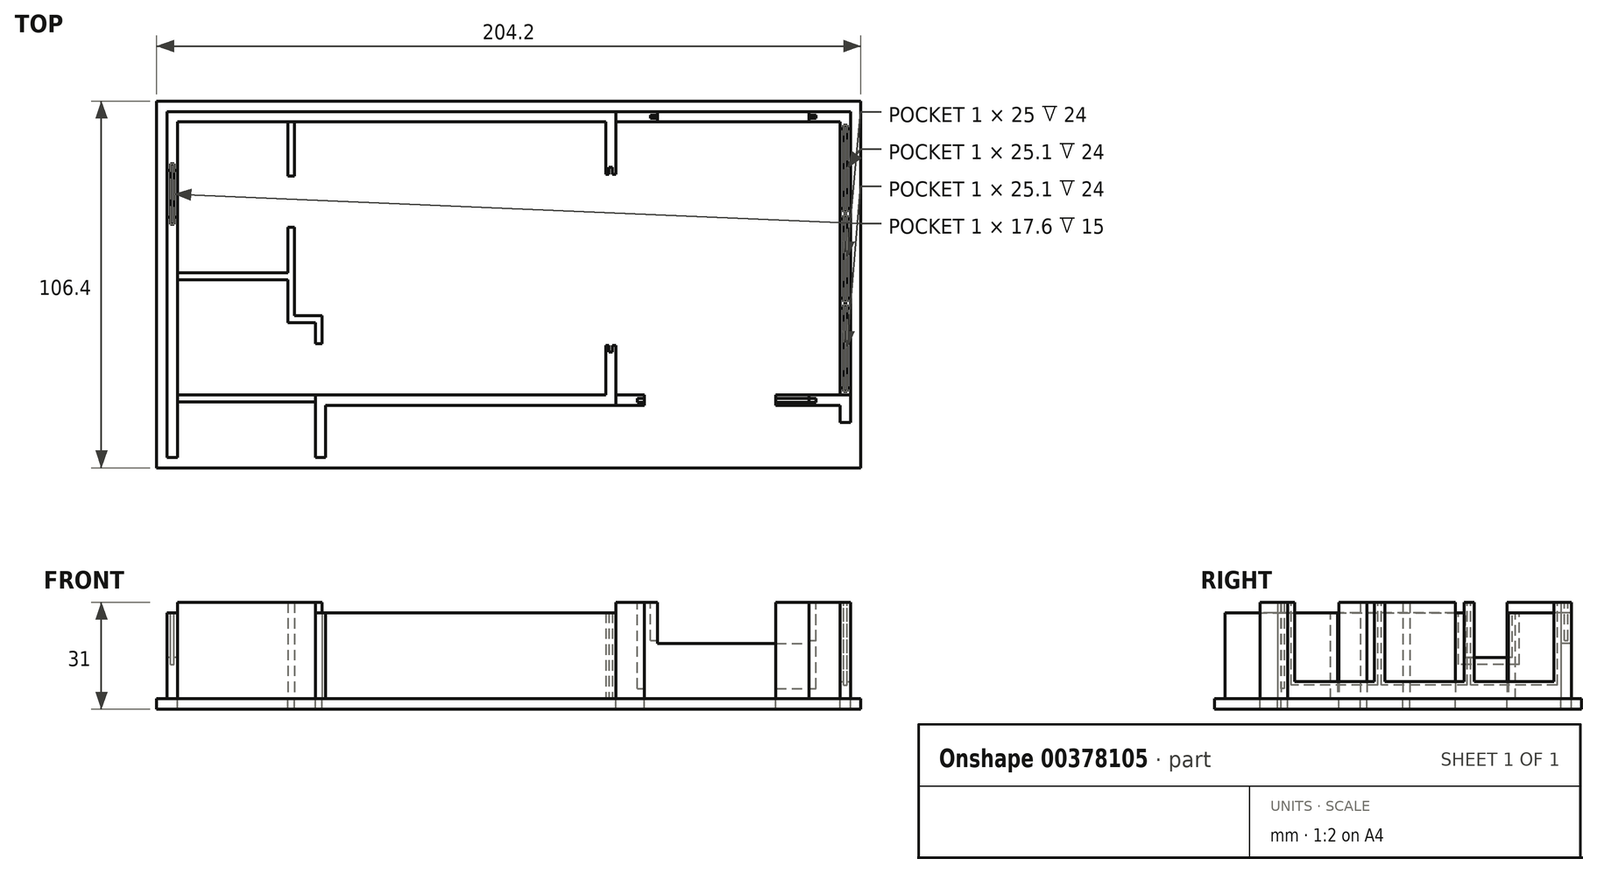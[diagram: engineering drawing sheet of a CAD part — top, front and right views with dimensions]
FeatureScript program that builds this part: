
annotation { "Feature Type Name" : "Feature", "Feature Type Description" : "" }
export const myFeature = defineFeature(function(context is Context, id is Id, definition is map)
    precondition{}
    {
        {
            var Q0;
            Q0=qCreatedBy(makeId("Top.planeOp"),FACE);
            var sketch = newSketch(context, id + "F0", { "sketchPlane" : qUnion([Q0])});
            skLineSegment(sketch, "E0.bottom", {"start": v(-6, 6) * mm, "end": v(198.2, 6) * mm});
            skLineSegment(sketch, "E0.top", {"start": v(-6, -100.4) * mm, "end": v(198.2, -100.4) * mm});
            skLineSegment(sketch, "E0.left", {"start": v(-6, 6) * mm, "end": v(-6, -100.4) * mm});
            skLineSegment(sketch, "E0.right", {"start": v(198.2, 6) * mm, "end": v(198.2, -100.4) * mm});
            skSolve(sketch);
        }
        {
            var Q0;
            Q0 = qSketchRegion(id + "F0", true);
            extrude(context, id + "F1", {"entities" : qUnion([Q0]), "oppositeDirection" : true, "depth" : 3 * mm});
        }
        {
            var Q0;
            Q0=qCreatedBy(makeId("Top.planeOp"),FACE);
            var sketch = newSketch(context, id + "F2", { "sketchPlane" : qUnion([Q0])});
            skLineSegment(sketch, "E1.bottom", {"start": v(0, 0) * mm, "end": v(124.2, 0) * mm});
            skLineSegment(sketch, "E1.top", {"start": v(40, -79.2) * mm, "end": v(124.2, -79.2) * mm});
            skLineSegment(sketch, "E1.left", {"start": v(0, 0) * mm, "end": v(0, -79.2) * mm});
            skLineSegment(sketch, "E2", {"start": v(124.2, 0) * mm, "end": v(124.2, -15.2) * mm});
            skLineSegment(sketch, "E3", {"start": v(124.2, -79.2) * mm, "end": v(124.2, -64.8) * mm});
            skLineSegment(sketch, "E4", {"start": v(0, -43.8) * mm, "end": v(34, -43.8) * mm, "construction": true});
            skLineSegment(sketch, "E5", {"start": v(34, -43.8) * mm, "end": v(34, -30.6) * mm, "construction": true});
            skLineSegment(sketch, "E6", {"start": v(34, 0) * mm, "end": v(34, -15.6) * mm, "construction": true});
            skLineSegment(sketch, "E7", {"start": v(34, -43.8) * mm, "end": v(34, -56.2) * mm, "construction": true});
            skLineSegment(sketch, "E8", {"start": v(0, -56.2) * mm, "end": v(40, -56.2) * mm, "construction": true});
            skLineSegment(sketch, "E9", {"start": v(40, -56.2) * mm, "end": v(40, -64.4) * mm, "construction": true});
            skLineSegment(sketch, "E10", {"start": v(40, -79.2) * mm, "end": v(40, -97.4) * mm});
            skLineSegment(sketch, "E11", {"start": v(0, -79.2) * mm, "end": v(0, -97.4) * mm});
            skLineSegment(sketch, "E12", {"start": v(0, -97.4) * mm, "end": v(40, -97.4) * mm, "construction": true});
            skLineSegment(sketch, "E13.0", {"start": v(-3, 3) * mm, "end": v(127.2, 3) * mm});
            skLineSegment(sketch, "E14.0", {"start": v(-3, 0) * mm, "end": v(-3, -79.2) * mm});
            skLineSegment(sketch, "E15.0", {"start": v(-3, -79.2) * mm, "end": v(-3, -97.4) * mm});
            skLineSegment(sketch, "E16.0", {"start": v(43, -82.2) * mm, "end": v(43, -97.4) * mm});
            skLineSegment(sketch, "E17.0", {"start": v(43, -82.2) * mm, "end": v(127.2, -82.2) * mm});
            skLineSegment(sketch, "E18.0", {"start": v(127.2, -82.34) * mm, "end": v(127.2, -64.8) * mm});
            skLineSegment(sketch, "E19", {"start": v(-3, -97.4) * mm, "end": v(0, -97.4) * mm});
            skLineSegment(sketch, "E20", {"start": v(40, -97.4) * mm, "end": v(43, -97.4) * mm});
            skLineSegment(sketch, "E21.0", {"start": v(127.2, 3.04) * mm, "end": v(127.2, -15.2) * mm});
            skLineSegment(sketch, "E22", {"start": v(124.2, -15.2) * mm, "end": v(127.2, -15.2) * mm});
            skLineSegment(sketch, "E23", {"start": v(-3, 0) * mm, "end": v(-3, 3) * mm});
            skPoint(sketch, "E24.orphan", {"position": v(0, 3) * mm});
            skLineSegment(sketch, "E25", {"start": v(124.2, -64.8) * mm, "end": v(127.2, -64.8) * mm});
            skSolve(sketch);
        }
        {
            var Q0;
            Q0=makeQuery(id+"F2.imprint","IMPRINT",FACE,{"disambiguationData":[TD([[makeQuery(id+"F2.imprint","IMPRINT",EDGE,{"derivedFrom":sQuery(id+"F2.wireOp",EDGE,"E1.bottom")}),1.0]])]});
            var Q1;
            Q1=makeQuery(id+"F2.imprint","IMPRINT",FACE,{"disambiguationData":[TD([[makeQuery(id+"F2.imprint","IMPRINT",EDGE,{"derivedFrom":sQuery(id+"F2.wireOp",EDGE,"E1.top")}),-1.0]])]});
            extrude(context, id + "F3", {"entities" : qUnion([Q0, Q1]), "operationType" : NewBodyOperationType.ADD, "depth" : 25 * mm});
        }
        {
            var Q0;
            Q0=qCreatedBy(makeId("Top.planeOp"),FACE);
            var sketch = newSketch(context, id + "F4", { "sketchPlane" : qUnion([Q0])});
            skLineSegment(sketch, "E26", {"start": v(0, -43.8) * mm, "end": v(32, -43.8) * mm});
            skLineSegment(sketch, "E27", {"start": v(34, 0) * mm, "end": v(34, -15.65) * mm});
            skLineSegment(sketch, "E28", {"start": v(34, -30.6) * mm, "end": v(34, -56.2) * mm});
            skLineSegment(sketch, "E29", {"start": v(34, -56.2) * mm, "end": v(42, -56.2) * mm});
            skLineSegment(sketch, "E30.0", {"start": v(32, 0) * mm, "end": v(32, -15.65) * mm});
            skLineSegment(sketch, "E31", {"start": v(32, 0) * mm, "end": v(34, 0) * mm});
            skLineSegment(sketch, "E32", {"start": v(32, -15.65) * mm, "end": v(34, -15.65) * mm});
            skLineSegment(sketch, "E33.0", {"start": v(32, -30.6) * mm, "end": v(32, -43.8) * mm});
            skLineSegment(sketch, "E34.0", {"start": v(0, -45.8) * mm, "end": v(32, -45.8) * mm});
            skLineSegment(sketch, "E35.0", {"start": v(32, -58.2) * mm, "end": v(40, -58.2) * mm});
            skLineSegment(sketch, "E36", {"start": v(32, -30.6) * mm, "end": v(34, -30.6) * mm});
            skLineSegment(sketch, "E37", {"start": v(0, -43.8) * mm, "end": v(0, -45.8) * mm});
            skPoint(sketch, "E38.orphan", {"position": v(34, -43.8) * mm});
            skLineSegment(sketch, "E39.trimOffspring", {"start": v(32, -45.8) * mm, "end": v(32, -58.2) * mm});
            skPoint(sketch, "E40.orphan", {"position": v(0, -56.2) * mm});
            skLineSegment(sketch, "E41.0", {"start": v(42, -56.2) * mm, "end": v(42, -64.4) * mm});
            skLineSegment(sketch, "E42", {"start": v(40, -64.4) * mm, "end": v(40, -58.2) * mm});
            skLineSegment(sketch, "E43", {"start": v(40, -64.4) * mm, "end": v(42, -64.4) * mm});
            skSolve(sketch);
        }
        {
            var Q0;
            Q0=makeQuery(id+"F4.imprint","IMPRINT",FACE,{"disambiguationData":[TD([[makeQuery(id+"F4.imprint","IMPRINT",EDGE,{"derivedFrom":sQuery(id+"F4.wireOp",EDGE,"E26")}),-1.0]])]});
            var Q1;
            Q1=makeQuery(id+"F4.imprint","IMPRINT",FACE,{"disambiguationData":[TD([[makeQuery(id+"F4.imprint","IMPRINT",EDGE,{"derivedFrom":sQuery(id+"F4.wireOp",EDGE,"E27")}),-1.0]])]});
            extrude(context, id + "F5", {"entities" : qUnion([Q0, Q1]), "depth" : 28 * mm});
        }
        {
            var Q0;
            Q0=qCreatedBy(makeId("Top.planeOp"),FACE);
            var sketch = newSketch(context, id + "F6", { "sketchPlane" : qUnion([Q0])});
            skLineSegment(sketch, "E44", {"start": v(127.2, -82.2) * mm, "end": v(135.4, -82.2) * mm});
            skLineSegment(sketch, "E45", {"start": v(183.2, -82.2) * mm, "end": v(192.2, -82.2) * mm});
            skLineSegment(sketch, "E46", {"start": v(192.2, -82.2) * mm, "end": v(192.2, -87.2) * mm});
            skLineSegment(sketch, "E47.0", {"start": v(127.2, -79.2) * mm, "end": v(135.4, -79.2) * mm});
            skLineSegment(sketch, "E48", {"start": v(135.4, -79.2) * mm, "end": v(135.4, -82.2) * mm});
            skLineSegment(sketch, "E49.0", {"start": v(183.2, -79.2) * mm, "end": v(195.2, -79.2) * mm});
            skLineSegment(sketch, "E50.0", {"start": v(195.2, -79.2) * mm, "end": v(195.2, -87.2) * mm});
            skLineSegment(sketch, "E51", {"start": v(183.2, -79.2) * mm, "end": v(183.2, -82.2) * mm});
            skLineSegment(sketch, "E52", {"start": v(192.2, -87.2) * mm, "end": v(195.2, -87.2) * mm});
            skLineSegment(sketch, "E53", {"start": v(127.2, -79.2) * mm, "end": v(127.2, -82.2) * mm});
            skSolve(sketch);
        }
        {
            var Q0;
            Q0=makeQuery(id+"F6.imprint","IMPRINT",FACE,{"disambiguationData":[TD([[makeQuery(id+"F6.imprint","IMPRINT",EDGE,{"derivedFrom":sQuery(id+"F6.wireOp",EDGE,"E45")}),1.0]])]});
            var Q1;
            Q1=makeQuery(id+"F6.imprint","IMPRINT",FACE,{"disambiguationData":[TD([[makeQuery(id+"F6.imprint","IMPRINT",EDGE,{"derivedFrom":sQuery(id+"F6.wireOp",EDGE,"E44")}),1.0]])]});
            extrude(context, id + "F7", {"entities" : qUnion([Q0, Q1]), "depth" : 28 * mm});
        }
        {
            var Q0;
            Q0=makeQuery(id+"F3.opExtrude","SWEPT_FACE",FACE,{"disambiguationData":[OSD([sQuery(id+"F2.wireOp",EDGE,"E14.0"),sQuery(id+"F2.wireOp",EDGE,"E15.0"),sQuery(id+"F2.wireOp",EDGE,"E23")])]});
            var sketch = newSketch(context, id + "F8", { "sketchPlane" : qUnion([Q0])});
            skLineSegment(sketch, "E54.bottom", {"start": v(14.1, 25) * mm, "end": v(27.7, 25) * mm});
            skLineSegment(sketch, "E54.top", {"start": v(14.1, 12) * mm, "end": v(27.7, 12) * mm});
            skLineSegment(sketch, "E54.left", {"start": v(14.1, 25) * mm, "end": v(14.1, 12) * mm});
            skLineSegment(sketch, "E54.right", {"start": v(27.7, 25) * mm, "end": v(27.7, 12) * mm});
            skSolve(sketch);
        }
        {
            var Q0;
            Q0 = qSketchRegion(id + "F8", true);
            extrude(context, id + "F9", {"entities" : qUnion([Q0]), "operationType" : NewBodyOperationType.REMOVE, "oppositeDirection" : true, "depth" : 3 * mm});
        }
        {
            var Q0;
            Q0=qCreatedBy(makeId("Top.planeOp"),FACE);
            var sketch = newSketch(context, id + "F10", { "sketchPlane" : qUnion([Q0])});
            skLineSegment(sketch, "E55.bottom", {"start": v(40, -79.2) * mm, "end": v(0, -79.2) * mm});
            skLineSegment(sketch, "E55.top", {"start": v(40, -81.2) * mm, "end": v(0, -81.2) * mm});
            skLineSegment(sketch, "E55.left", {"start": v(40, -79.2) * mm, "end": v(40, -81.2) * mm});
            skLineSegment(sketch, "E55.right", {"start": v(0, -79.2) * mm, "end": v(0, -81.2) * mm});
            skSolve(sketch);
        }
        {
            var Q0;
            Q0=makeQuery(id+"F10.imprint","IMPRINT",FACE,{"disambiguationData":[TD([[makeQuery(id+"F10.imprint","IMPRINT",EDGE,{"derivedFrom":sQuery(id+"F10.wireOp",EDGE,"E55.bottom")}),1.0]])]});
            extrude(context, id + "F11", {"entities" : qUnion([Q0]), "depth" : 28 * mm});
        }
        {
            var Q0;
            Q0=qCreatedBy(makeId("Top.planeOp"),FACE);
            var sketch = newSketch(context, id + "F12", { "sketchPlane" : qUnion([Q0])});
            skLineSegment(sketch, "E56.bottom", {"start": v(127.2, 3) * mm, "end": v(195.2, 3) * mm});
            skLineSegment(sketch, "E56.top", {"start": v(127.2, 0) * mm, "end": v(195.2, 0) * mm});
            skLineSegment(sketch, "E56.left", {"start": v(127.2, 3) * mm, "end": v(127.2, 0) * mm});
            skPoint(sketch, "E57.orphan", {"position": v(185.9, 0) * mm});
            skLineSegment(sketch, "E58", {"start": v(195.2, 0) * mm, "end": v(195.2, 3) * mm});
            skSolve(sketch);
        }
        {
            var Q0;
            Q0=makeQuery(id+"F12.imprint","IMPRINT",FACE,{"disambiguationData":[TD([[makeQuery(id+"F12.imprint","IMPRINT",EDGE,{"derivedFrom":sQuery(id+"F12.wireOp",EDGE,"E56.bottom")}),-1.0]])]});
            extrude(context, id + "F13", {"entities" : qUnion([Q0]), "depth" : 28 * mm});
        }
        {
            var Q0;
            Q0=makeQuery(id+"F13.opExtrude","SWEPT_FACE",FACE,{"disambiguationData":[OSD([sQuery(id+"F12.wireOp",EDGE,"E56.top")])]});
            var sketch = newSketch(context, id + "F14", { "sketchPlane" : qUnion([Q0])});
            skLineSegment(sketch, "E59.bottom", {"start": v(139.2, 28) * mm, "end": v(183.2, 28) * mm});
            skLineSegment(sketch, "E59.top", {"start": v(139.2, 16) * mm, "end": v(183.2, 16) * mm});
            skLineSegment(sketch, "E59.left", {"start": v(139.2, 28) * mm, "end": v(139.2, 16) * mm});
            skLineSegment(sketch, "E59.right", {"start": v(183.2, 28) * mm, "end": v(183.2, 16) * mm});
            skSolve(sketch);
        }
        {
            var Q0;
            Q0=makeQuery(id+"F14.imprint","IMPRINT",FACE,{"disambiguationData":[TD([[makeQuery(id+"F14.imprint","IMPRINT",EDGE,{"derivedFrom":sQuery(id+"F14.wireOp",EDGE,"E59.bottom")}),-1.0]])]});
            extrude(context, id + "F15", {"entities" : qUnion([Q0]), "operationType" : NewBodyOperationType.REMOVE, "oppositeDirection" : true, "depth" : 3 * mm});
        }
        {
            var Q0;
            Q0=qCreatedBy(makeId("Top.planeOp"),FACE);
            var sketch = newSketch(context, id + "F16", { "sketchPlane" : qUnion([Q0])});
            skLineSegment(sketch, "E60.bottom", {"start": v(192.2, 0) * mm, "end": v(195.2, 0) * mm});
            skLineSegment(sketch, "E60.top", {"start": v(192.2, -79.2) * mm, "end": v(195.2, -79.2) * mm});
            skLineSegment(sketch, "E60.left", {"start": v(192.2, 0) * mm, "end": v(192.2, -79.2) * mm});
            skLineSegment(sketch, "E60.right", {"start": v(195.2, 0) * mm, "end": v(195.2, -79.2) * mm});
            skSolve(sketch);
        }
        {
            var Q0;
            Q0=makeQuery(id+"F16.imprint","IMPRINT",FACE,{"disambiguationData":[TD([[makeQuery(id+"F16.imprint","IMPRINT",EDGE,{"derivedFrom":sQuery(id+"F16.wireOp",EDGE,"E60.bottom")}),-1.0]])]});
            extrude(context, id + "F17", {"entities" : qUnion([Q0]), "depth" : 5 * mm});
        }
        {
            var Q0;
            Q0=makeQuery(id+"F17.opExtrude","CAP_FACE",FACE,{"disambiguationData":[OSD([sQuery(id+"F16.wireOp",EDGE,"E60.bottom"),sQuery(id+"F16.wireOp",EDGE,"E60.top"),sQuery(id+"F16.wireOp",EDGE,"E60.left"),sQuery(id+"F16.wireOp",EDGE,"E60.right")])],"isStart":false});
            var sketch = newSketch(context, id + "F18", { "sketchPlane" : qUnion([Q0])});
            skLineSegment(sketch, "E61.bottom", {"start": v(192.2, 0) * mm, "end": v(195.2, 0) * mm});
            skLineSegment(sketch, "E61.top", {"start": v(192.2, -2) * mm, "end": v(195.2, -2) * mm});
            skLineSegment(sketch, "E61.left", {"start": v(192.2, 0) * mm, "end": v(192.2, -2) * mm});
            skLineSegment(sketch, "E61.right", {"start": v(195.2, 0) * mm, "end": v(195.2, -2) * mm});
            skLineSegment(sketch, "E62.bottom", {"start": v(192.2, -79.2) * mm, "end": v(195.2, -79.2) * mm});
            skLineSegment(sketch, "E62.top", {"start": v(192.2, -77.2) * mm, "end": v(195.2, -77.2) * mm});
            skLineSegment(sketch, "E62.left", {"start": v(192.2, -79.2) * mm, "end": v(192.2, -77.2) * mm});
            skLineSegment(sketch, "E62.right", {"start": v(195.2, -79.2) * mm, "end": v(195.2, -77.2) * mm});
            skLineSegment(sketch, "E63.bottom", {"start": v(192.2, -54.1) * mm, "end": v(195.2, -54.1) * mm});
            skLineSegment(sketch, "E63.top", {"start": v(192.2, -51.1) * mm, "end": v(195.2, -51.1) * mm});
            skLineSegment(sketch, "E63.left", {"start": v(192.2, -54.1) * mm, "end": v(192.2, -51.1) * mm});
            skLineSegment(sketch, "E63.right", {"start": v(195.2, -54.1) * mm, "end": v(195.2, -51.1) * mm});
            skLineSegment(sketch, "E64.bottom", {"start": v(192.2, -28.1) * mm, "end": v(195.2, -28.1) * mm});
            skLineSegment(sketch, "E64.top", {"start": v(192.2, -25.1) * mm, "end": v(195.2, -25.1) * mm});
            skLineSegment(sketch, "E64.left", {"start": v(192.2, -28.1) * mm, "end": v(192.2, -25.1) * mm});
            skLineSegment(sketch, "E64.right", {"start": v(195.2, -28.1) * mm, "end": v(195.2, -25.1) * mm});
            skSolve(sketch);
        }
        {
            var Q0;
            Q0 = qSketchRegion(id + "F18", true);
            extrude(context, id + "F19", {"entities" : qUnion([Q0]), "operationType" : NewBodyOperationType.ADD, "depth" : 23 * mm});
        }
        {
            var Q0;
            {var subQ0=sQuery(id+"F2.wireOp",EDGE,"E2");var subQ1=sQuery(id+"F2.wireOp",EDGE,"E22");var subQ2=sQuery(id+"F2.wireOp",EDGE,"E11");var subQ3=sQuery(id+"F2.wireOp",EDGE,"E1.left");var subQ4=sQuery(id+"F2.wireOp",EDGE,"E21.0");var subQ5=sQuery(id+"F2.wireOp",EDGE,"E13.0");var subQ6=sQuery(id+"F2.wireOp",EDGE,"E1.bottom");var subQ7=sQuery(id+"F2.wireOp",EDGE,"E23");var subQ8=sQuery(id+"F2.wireOp",EDGE,"E15.0");var subQ9=sQuery(id+"F2.wireOp",EDGE,"E14.0");Q0=makeQuery(id+"F9.boolean.opBoolean","SPLIT",FACE,{"disambiguationData":[TD([makeQuery(id+"F3.opExtrude","SWEPT_FACE",FACE,{"disambiguationData":[OSD([subQ6])]})])],"derivedFrom":makeQuery(id+"F3.opExtrude","CAP_FACE",FACE,{"disambiguationData":[OSD([subQ6,subQ3,subQ0,subQ2,subQ5,subQ9,subQ8,sQuery(id+"F2.wireOp",EDGE,"E19"),subQ4,subQ1,subQ7])],"isStart":false})});}
            var sketch = newSketch(context, id + "F20", { "sketchPlane" : qUnion([Q0])});
            skPoint(sketch, "E65.oppositeSnap0", {"position": v(-1, -14.1) * mm});
            skLineSegment(sketch, "E65.bottom", {"start": v(-2, -12.1) * mm, "end": v(-1, -12.1) * mm});
            skLineSegment(sketch, "E65.top", {"start": v(-2, -29.7) * mm, "end": v(-1, -29.7) * mm});
            skLineSegment(sketch, "E65.left", {"start": v(-2, -12.1) * mm, "end": v(-2, -29.7) * mm});
            skLineSegment(sketch, "E65.right", {"start": v(-1, -12.1) * mm, "end": v(-1, -29.7) * mm});
            skSolve(sketch);
        }
        {
            var Q0;
            {var subQ0=sQuery(id+"F20.wireOp",EDGE,"E65.bottom");Q0=makeQuery(id+"F20.imprint","IMPRINT",FACE,{"disambiguationData":[TD([[makeQuery(id+"F20.imprint","IMPRINT",EDGE,{"derivedFrom":subQ0}),-1.0]])]});}
            var Q1;
            {var subQ0=sQuery(id+"F20.wireOp",EDGE,"E65.top");Q1=makeQuery(id+"F20.imprint","IMPRINT",FACE,{"disambiguationData":[TD([[makeQuery(id+"F20.imprint","IMPRINT",EDGE,{"derivedFrom":subQ0}),1.0]])]});}
            extrude(context, id + "F21", {"entities" : qUnion([Q0, Q1]), "operationType" : NewBodyOperationType.REMOVE, "oppositeDirection" : true, "depth" : 15 * mm});
        }
        {
            var Q0;
            Q0=makeQuery(id+"F3.opExtrude","CAP_FACE",FACE,{"disambiguationData":[OSD([sQuery(id+"F2.wireOp",EDGE,"E1.top"),sQuery(id+"F2.wireOp",EDGE,"E3"),sQuery(id+"F2.wireOp",EDGE,"E10"),sQuery(id+"F2.wireOp",EDGE,"E16.0"),sQuery(id+"F2.wireOp",EDGE,"E17.0"),sQuery(id+"F2.wireOp",EDGE,"E18.0"),sQuery(id+"F2.wireOp",EDGE,"E20"),sQuery(id+"F2.wireOp",EDGE,"E25")])],"isStart":false});
            var sketch = newSketch(context, id + "F22", { "sketchPlane" : qUnion([Q0])});
            skPoint(sketch, "E66.oppositeSnap0", {"position": v(126.2, -64.8) * mm});
            skLineSegment(sketch, "E66.bottom", {"start": v(125.2, -66.8) * mm, "end": v(126.2, -66.8) * mm});
            skLineSegment(sketch, "E66.top", {"start": v(125.2, -13.2) * mm, "end": v(126.2, -13.2) * mm});
            skLineSegment(sketch, "E66.left", {"start": v(125.2, -66.8) * mm, "end": v(125.2, -13.2) * mm});
            skLineSegment(sketch, "E66.right", {"start": v(126.2, -66.8) * mm, "end": v(126.2, -13.2) * mm});
            skSolve(sketch);
        }
        {
            var Q0;
            Q0=makeQuery(id+"F22.imprint","IMPRINT",FACE,{"disambiguationData":[TD([[makeQuery(id+"F22.imprint","IMPRINT",EDGE,{"derivedFrom":sQuery(id+"F22.wireOp",EDGE,"TBzw3mYv-Q210-kkmf-RxrV-h13io9Ekoqw2.bottom")}),1.0]])]});
            var Q1;
            {var subQ0=sQuery(id+"F22.wireOp",EDGE,"E66.bottom");Q1=makeQuery(id+"F22.imprint","IMPRINT",FACE,{"disambiguationData":[TD([[makeQuery(id+"F22.imprint","IMPRINT",EDGE,{"derivedFrom":subQ0}),1.0]])]});}
            var Q2;
            {var subQ0=sQuery(id+"F22.wireOp",EDGE,"E66.top");Q2=makeQuery(id+"F22.imprint","IMPRINT",FACE,{"disambiguationData":[TD([[makeQuery(id+"F22.imprint","IMPRINT",EDGE,{"derivedFrom":subQ0}),-1.0]])]});}
            extrude(context, id + "F23", {"entities" : qUnion([Q0, Q1, Q2]), "operationType" : NewBodyOperationType.REMOVE, "oppositeDirection" : true, "depth" : 25 * mm});
        }
        {
            var Q0;
            {var subQ0=sQuery(id+"F12.wireOp",EDGE,"E56.bottom");var subQ1=sQuery(id+"F12.wireOp",EDGE,"E58");var subQ2=sQuery(id+"F12.wireOp",EDGE,"E56.top");Q0=makeQuery(id+"F15.boolean.opBoolean","SPLIT",FACE,{"disambiguationData":[TD([makeQuery(id+"F13.opExtrude","SWEPT_FACE",FACE,{"disambiguationData":[OSD([subQ1])]})])],"derivedFrom":makeQuery(id+"F13.opExtrude","CAP_FACE",FACE,{"disambiguationData":[OSD([subQ0,subQ2,sQuery(id+"F12.wireOp",EDGE,"E56.left"),subQ1])],"isStart":false})});}
            var sketch = newSketch(context, id + "F24", { "sketchPlane" : qUnion([Q0])});
            skLineSegment(sketch, "E67.bottom", {"start": v(137.2, 1) * mm, "end": v(185.2, 1) * mm});
            skLineSegment(sketch, "E67.top", {"start": v(137.2, 2) * mm, "end": v(185.2, 2) * mm});
            skLineSegment(sketch, "E67.left", {"start": v(137.2, 1) * mm, "end": v(137.2, 2) * mm});
            skLineSegment(sketch, "E67.right", {"start": v(185.2, 1) * mm, "end": v(185.2, 2) * mm});
            skSolve(sketch);
        }
        {
            var Q0;
            {var subQ0=sQuery(id+"F24.wireOp",EDGE,"E67.left");Q0=makeQuery(id+"F24.imprint","IMPRINT",FACE,{"disambiguationData":[TD([[makeQuery(id+"F24.imprint","IMPRINT",EDGE,{"derivedFrom":subQ0}),-1.0]])]});}
            var Q1;
            {var subQ0=sQuery(id+"F24.wireOp",EDGE,"E67.right");Q1=makeQuery(id+"F24.imprint","IMPRINT",FACE,{"disambiguationData":[TD([[makeQuery(id+"F24.imprint","IMPRINT",EDGE,{"derivedFrom":subQ0}),1.0]])]});}
            extrude(context, id + "F25", {"entities" : qUnion([Q0, Q1]), "operationType" : NewBodyOperationType.REMOVE, "oppositeDirection" : true, "depth" : 11 * mm});
        }
        {
            var Q0;
            Q0=makeQuery(id+"F19.opExtrude","CAP_FACE",FACE,{"disambiguationData":[OSD([sQuery(id+"F18.wireOp",EDGE,"E63.bottom"),sQuery(id+"F18.wireOp",EDGE,"E63.top"),sQuery(id+"F18.wireOp",EDGE,"E63.left"),sQuery(id+"F18.wireOp",EDGE,"E63.right")])],"isStart":false});
            var sketch = newSketch(context, id + "F26", { "sketchPlane" : qUnion([Q0])});
            skSolve(sketch);
        }
        {
            var Q0;
            Q0=makeQuery(id+"F26.imprint","IMPRINT",FACE,{"disambiguationData":[TD([[makeQuery(id+"F26.imprint","IMPRINT",EDGE,{"derivedFrom":makeQuery(id+"F19.opExtrude","CAP_EDGE",EDGE,{"disambiguationData":[OSD([sQuery(id+"F18.wireOp",EDGE,"E63.bottom")])],"isStart":false})}),1.0]])]});
            var sketch = newSketch(context, id + "F27", { "sketchPlane" : qUnion([Q0])});
            skLineSegment(sketch, "E68.bottom", {"start": v(193.2, -1) * mm, "end": v(194.2, -1) * mm});
            skLineSegment(sketch, "E68.top", {"start": v(193.2, -26.1) * mm, "end": v(194.2, -26.1) * mm});
            skLineSegment(sketch, "E68.left", {"start": v(193.2, -1) * mm, "end": v(193.2, -26.1) * mm});
            skLineSegment(sketch, "E68.right", {"start": v(194.2, -1) * mm, "end": v(194.2, -26.1) * mm});
            skLineSegment(sketch, "E69.bottom", {"start": v(193.2, -27.1) * mm, "end": v(194.2, -27.1) * mm});
            skLineSegment(sketch, "E69.top", {"start": v(193.2, -52.1) * mm, "end": v(194.2, -52.1) * mm});
            skLineSegment(sketch, "E69.left", {"start": v(193.2, -27.1) * mm, "end": v(193.2, -52.1) * mm});
            skLineSegment(sketch, "E69.right", {"start": v(194.2, -27.1) * mm, "end": v(194.2, -52.1) * mm});
            skLineSegment(sketch, "E70.bottom", {"start": v(193.2, -53.1) * mm, "end": v(194.2, -53.1) * mm});
            skLineSegment(sketch, "E70.top", {"start": v(193.2, -78.2) * mm, "end": v(194.2, -78.2) * mm});
            skLineSegment(sketch, "E70.left", {"start": v(193.2, -53.1) * mm, "end": v(193.2, -78.2) * mm});
            skLineSegment(sketch, "E70.right", {"start": v(194.2, -53.1) * mm, "end": v(194.2, -78.2) * mm});
            skSolve(sketch);
        }
        {
            var Q0;
            Q0 = qSketchRegion(id + "F27", true);
            extrude(context, id + "F28", {"entities" : qUnion([Q0]), "operationType" : NewBodyOperationType.REMOVE, "oppositeDirection" : true, "depth" : 24 * mm});
        }
        {
            var Q0;
            Q0=qCreatedBy(makeId("Top.planeOp"),FACE);
            var sketch = newSketch(context, id + "F29", { "sketchPlane" : qUnion([Q0])});
            skLineSegment(sketch, "E71", {"start": v(195.2, -87.2) * mm, "end": v(195.2, -79.2) * mm});
            skLineSegment(sketch, "E72", {"start": v(195.2, -79.2) * mm, "end": v(173.6, -79.2) * mm});
            skLineSegment(sketch, "E73", {"start": v(173.6, -79.2) * mm, "end": v(173.6, -82.2) * mm});
            skLineSegment(sketch, "E74", {"start": v(173.6, -82.2) * mm, "end": v(192.2, -82.2) * mm});
            skLineSegment(sketch, "E75", {"start": v(192.2, -82.2) * mm, "end": v(192.2, -87.2) * mm});
            skLineSegment(sketch, "E76", {"start": v(192.2, -87.2) * mm, "end": v(195.2, -87.2) * mm});
            skSolve(sketch);
        }
        {
            var Q0;
            Q0=makeQuery(id+"F29.imprint","IMPRINT",FACE,{"disambiguationData":[TD([[makeQuery(id+"F29.imprint","IMPRINT",EDGE,{"derivedFrom":sQuery(id+"F29.wireOp",EDGE,"E71")}),1.0]])]});
            extrude(context, id + "F30", {"entities" : qUnion([Q0]), "depth" : 28 * mm});
        }
        {
            var Q0;
            Q0=makeQuery(id+"F7.opExtrude","CAP_FACE",FACE,{"disambiguationData":[OSD([sQuery(id+"F6.wireOp",EDGE,"E44"),sQuery(id+"F6.wireOp",EDGE,"E47.0"),sQuery(id+"F6.wireOp",EDGE,"E48"),sQuery(id+"F6.wireOp",EDGE,"E53")])],"isStart":false});
            var sketch = newSketch(context, id + "F31", { "sketchPlane" : qUnion([Q0])});
            skLineSegment(sketch, "E77.bottom", {"start": v(133.4, -81.31) * mm, "end": v(185.2, -81.31) * mm});
            skLineSegment(sketch, "E77.top", {"start": v(133.4, -80.2) * mm, "end": v(185.2, -80.2) * mm});
            skLineSegment(sketch, "E77.left", {"start": v(133.4, -81.31) * mm, "end": v(133.4, -80.2) * mm});
            skLineSegment(sketch, "E77.right", {"start": v(185.2, -81.31) * mm, "end": v(185.2, -80.2) * mm});
            skSolve(sketch);
        }
        {
            var Q0;
            {var subQ0=sQuery(id+"F31.wireOp",EDGE,"E77.right");Q0=makeQuery(id+"F31.imprint","IMPRINT",FACE,{"disambiguationData":[TD([[makeQuery(id+"F31.imprint","IMPRINT",EDGE,{"derivedFrom":subQ0}),1.0]])]});}
            var Q1;
            {var subQ0=sQuery(id+"F31.wireOp",EDGE,"E77.left");Q1=makeQuery(id+"F31.imprint","IMPRINT",FACE,{"disambiguationData":[TD([[makeQuery(id+"F31.imprint","IMPRINT",EDGE,{"derivedFrom":subQ0}),-1.0]])]});}
            extrude(context, id + "F32", {"entities" : qUnion([Q0, Q1]), "operationType" : NewBodyOperationType.REMOVE, "oppositeDirection" : true, "depth" : 25 * mm});
        }
        {
            var Q0;
            Q0=makeQuery(id+"F23.boolean.opBoolean","MERGE",FACE,{"derivedFrom":[makeQuery(id+"F1.opExtrude","CAP_FACE",FACE,{"disambiguationData":[OSD([sQuery(id+"F0.wireOp",EDGE,"E0.bottom"),sQuery(id+"F0.wireOp",EDGE,"E0.top"),sQuery(id+"F0.wireOp",EDGE,"E0.left"),sQuery(id+"F0.wireOp",EDGE,"E0.right")])],"isStart":true}),makeQuery(id+"F23.opExtrude","CAP_FACE",FACE,{"disambiguationData":[OSD([sQuery(id+"F22.wireOp",EDGE,"E66.bottom"),sQuery(id+"F22.wireOp",EDGE,"E66.top"),sQuery(id+"F22.wireOp",EDGE,"E66.left"),sQuery(id+"F22.wireOp",EDGE,"E66.right")])],"isStart":false})]});
            var sketch = newSketch(context, id + "F33", { "sketchPlane" : qUnion([Q0])});
            skLineSegment(sketch, "E78", {"start": v(0, -43.8) * mm, "end": v(32, -43.8) * mm});
            skLineSegment(sketch, "E79", {"start": v(32, -43.8) * mm, "end": v(32, -30.6) * mm});
            skLineSegment(sketch, "E80", {"start": v(32, -30.6) * mm, "end": v(34, -30.6) * mm});
            skLineSegment(sketch, "E81", {"start": v(34, -30.6) * mm, "end": v(34, -56.2) * mm});
            skLineSegment(sketch, "E82", {"start": v(34, -56.2) * mm, "end": v(42, -56.2) * mm});
            skLineSegment(sketch, "E83", {"start": v(42, -56.2) * mm, "end": v(42, -64.4) * mm});
            skLineSegment(sketch, "E84", {"start": v(42, -64.4) * mm, "end": v(40, -64.4) * mm});
            skLineSegment(sketch, "E85", {"start": v(40, -64.4) * mm, "end": v(40, -58.2) * mm});
            skLineSegment(sketch, "E86", {"start": v(40, -58.2) * mm, "end": v(32, -58.2) * mm});
            skLineSegment(sketch, "E87", {"start": v(32, -58.2) * mm, "end": v(32, -45.8) * mm});
            skLineSegment(sketch, "E88", {"start": v(32, -45.8) * mm, "end": v(0, -45.8) * mm});
            skLineSegment(sketch, "E89", {"start": v(0, -45.8) * mm, "end": v(0, -43.8) * mm});
            skLineSegment(sketch, "E90.bottom", {"start": v(32, 0) * mm, "end": v(33.87, 0) * mm});
            skLineSegment(sketch, "E90.left", {"start": v(32, 0) * mm, "end": v(32, 0) * mm});
            skLineSegment(sketch, "E90.right", {"start": v(33.87, 0) * mm, "end": v(33.87, 0) * mm});
            skLineSegment(sketch, "E91.bottom", {"start": v(32, -15.65) * mm, "end": v(34, -15.65) * mm});
            skLineSegment(sketch, "E91.top", {"start": v(32, 0) * mm, "end": v(34, 0) * mm});
            skLineSegment(sketch, "E91.left", {"start": v(32, -15.65) * mm, "end": v(32, 0) * mm});
            skLineSegment(sketch, "E91.right", {"start": v(34, -15.65) * mm, "end": v(34, 0) * mm});
            skLineSegment(sketch, "E92.bottom", {"start": v(0, -81.2) * mm, "end": v(40, -81.2) * mm});
            skLineSegment(sketch, "E92.top", {"start": v(0, -79.2) * mm, "end": v(40, -79.2) * mm});
            skLineSegment(sketch, "E92.left", {"start": v(0, -81.2) * mm, "end": v(0, -79.2) * mm});
            skLineSegment(sketch, "E92.right", {"start": v(40, -81.2) * mm, "end": v(40, -79.2) * mm});
            skLineSegment(sketch, "E93", {"start": v(127.2, 3) * mm, "end": v(195.2, 3) * mm});
            skLineSegment(sketch, "E94", {"start": v(195.2, 3) * mm, "end": v(195.2, -87.2) * mm});
            skLineSegment(sketch, "E95", {"start": v(195.2, -87.2) * mm, "end": v(192.2, -87.2) * mm});
            skLineSegment(sketch, "E96", {"start": v(192.2, -87.2) * mm, "end": v(192.2, -82.2) * mm});
            skLineSegment(sketch, "E97", {"start": v(192.2, -82.2) * mm, "end": v(173.6, -82.2) * mm});
            skLineSegment(sketch, "E98", {"start": v(173.6, -82.2) * mm, "end": v(173.6, -79.2) * mm});
            skLineSegment(sketch, "E99", {"start": v(173.6, -79.2) * mm, "end": v(192.2, -79.2) * mm});
            skLineSegment(sketch, "E100", {"start": v(192.2, -79.2) * mm, "end": v(192.2, 0) * mm});
            skLineSegment(sketch, "E101", {"start": v(192.2, 0) * mm, "end": v(127.2, 0) * mm});
            skLineSegment(sketch, "E102", {"start": v(127.2, 0) * mm, "end": v(127.2, 3) * mm});
            skLineSegment(sketch, "E103.bottom", {"start": v(127.2, -82.2) * mm, "end": v(135.4, -82.2) * mm});
            skLineSegment(sketch, "E103.top", {"start": v(127.2, -79.2) * mm, "end": v(135.4, -79.2) * mm});
            skLineSegment(sketch, "E103.left", {"start": v(127.2, -82.2) * mm, "end": v(127.2, -79.2) * mm});
            skLineSegment(sketch, "E103.right", {"start": v(135.4, -82.2) * mm, "end": v(135.4, -79.2) * mm});
            skSolve(sketch);
        }
        {
            var Q0;
            Q0 = qSketchRegion(id + "F33", true);
            extrude(context, id + "F34", {"entities" : qUnion([Q0]), "operationType" : NewBodyOperationType.REMOVE, "endBound" : BoundingType.THROUGH_ALL, "oppositeDirection" : true, "depth" : 25 * mm});
        }
    });
